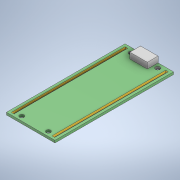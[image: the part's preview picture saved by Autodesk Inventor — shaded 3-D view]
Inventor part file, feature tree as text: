
AUTODESK INVENTOR PART (.ipt)
format: ipt  version: 2022 (Build 260153000, 153)  size: 157,184 bytes
history: native  units: in
note: dims shown in document units (in); Inventor stores cm internally (conversion verified against a paired STEP export)
features: extrude x3, sketch x3
ambient origin geometry x8: Origin, YZ Plane, XZ Plane, XY Plane, X Axis, Y Axis, Z Axis, Center Point
bodies: Solid1 (feature_tree)
feature tree (6):
  extrude  "Extrusion1"  Depth=2.02in
  extrude  "Extrusion2"  Depth=0.04in
  extrude  "Extrusion3"  Depth=0.1in
  sketch  "Sketch1"  dims[d0=0.827in d1=2.02in]
  sketch  "Sketch2"  dims[d2=0.045in d3=0.04in]
  sketch  "Sketch3"  dims[d4=0.045in d7=0.15in d8=0.037in d9=0.075in d10=0.075in d11=0.045in d12=0.15in d13=0.075in d14=0.075in d15=0.04in d16=0.0in d17=0.1in d18=0.0in d19=0.1in d20=0.0in]
